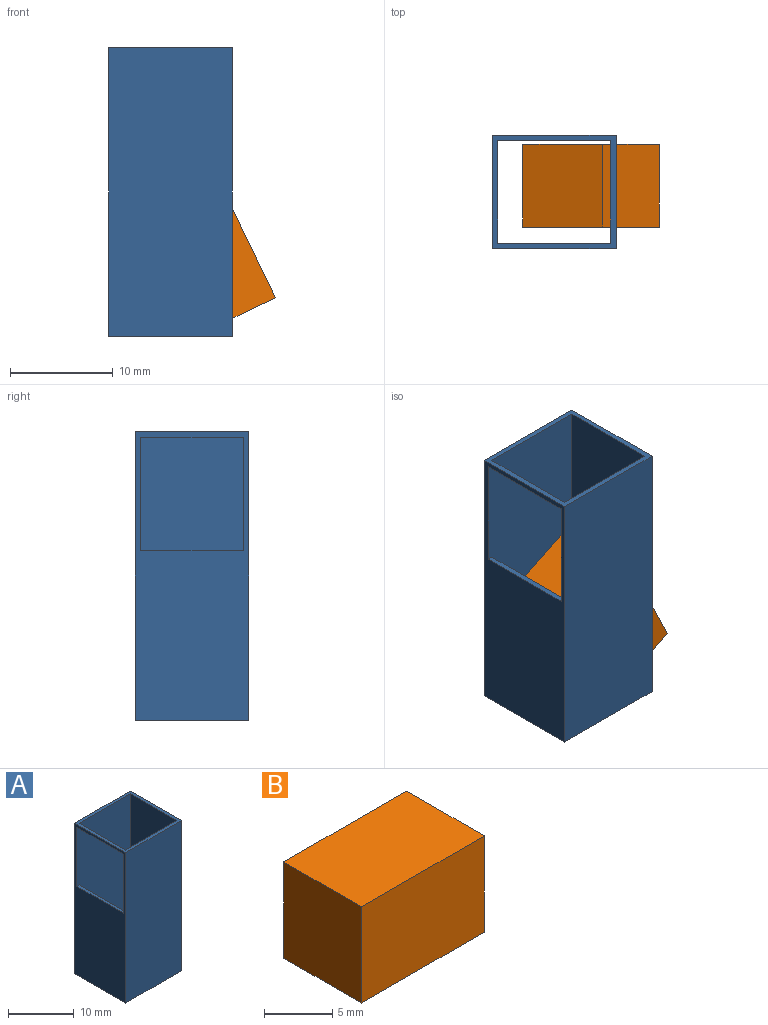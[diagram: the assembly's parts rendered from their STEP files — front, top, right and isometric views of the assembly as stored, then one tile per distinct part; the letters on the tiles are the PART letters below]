
ASSEMBLY  parts=2 mates=1
PART A: 14 faces, bbox 12x11x28 mm
  f0: plane 10x0.5mm, normal (1,0,0), area 5mm2, adj f5,f7,f9,f13
  f1: plane 17x10mm, normal (-1,0,0), area 170mm2, adj f5,f7,f9,f11
  f2: plane 28x11mm, normal (-1,0,0), area 198mm2, adj f3,f5,f7,f8,f9,f10,f12,f13
  f3: plane 28x12mm, normal (0,-1,0), area 336mm2, adj f2,f4,f9,f10
  f4: plane 28x11mm, normal (1,0,0), area 198mm2, adj f3,f5,f7,f8,f9,f10,f11
  f5: plane 28x12mm, normal (0,1,0), area 319mm2, adj f0,f1,f2,f4,f6,f9,f10,f11
  f6: plane 16.5x10mm, normal (1,0,0), area 165mm2, adj f5,f7,f10,f12
  f7: plane 28x12mm, normal (0,-1,0), area 319mm2, adj f0,f1,f2,f4,f6,f9,f10,f11
  f8: plane 28x12mm, normal (0,1,0), area 336mm2, adj f2,f4,f9,f10
  f9: plane 12x11mm, normal (0,0,1), area 22mm2, adj f0,f1,f2,f3,f4,f5,f7,f8
  f10: plane 12x11mm, normal (0,0,-1), area 17mm2, adj f2,f3,f4,f5,f6,f7,f8
  f11: plane 10x0.5mm, normal (0,0,-1), area 5mm2, adj f1,f4,f5,f7
  f12: plane 10x0.5mm, normal (0,0,1), area 5mm2, adj f2,f5,f6,f7
  f13: plane 10x0.5mm, normal (0,0,-1), area 5mm2, adj f0,f2,f5,f7
PART B: 6 faces, bbox 12.7x8x8.6 mm
  f0: plane 8.61x8.04mm, normal (-1,0,0), area 69.2mm2, adj f1,f3,f4,f5
  f1: plane 12.7x8.61mm, normal (0,-1,0), area 109.3mm2, adj f0,f2,f4,f5
  f2: plane 8.61x8.04mm, normal (1,0,0), area 69.2mm2, adj f1,f3,f4,f5
  f3: plane 12.7x8.61mm, normal (0,1,0), area 109.3mm2, adj f0,f2,f4,f5
  f4: plane 12.7x8.04mm, normal (0,0,1), area 102.1mm2, adj f0,f1,f2,f3
  f5: plane 12.7x8.04mm, normal (0,0,-1), area 102.1mm2, adj f0,f1,f2,f3
PLACE A t=(-13.71,4.61,1.56)mm fixed
PLACE B rot(axis=(0,1,0),64.3deg) t=(-1.06,-32.38,-23.09)mm
MATE parallel B.f1 <-> A.f3  axis (0,-1,0) through (-11.81,-1.3,9.15)mm
